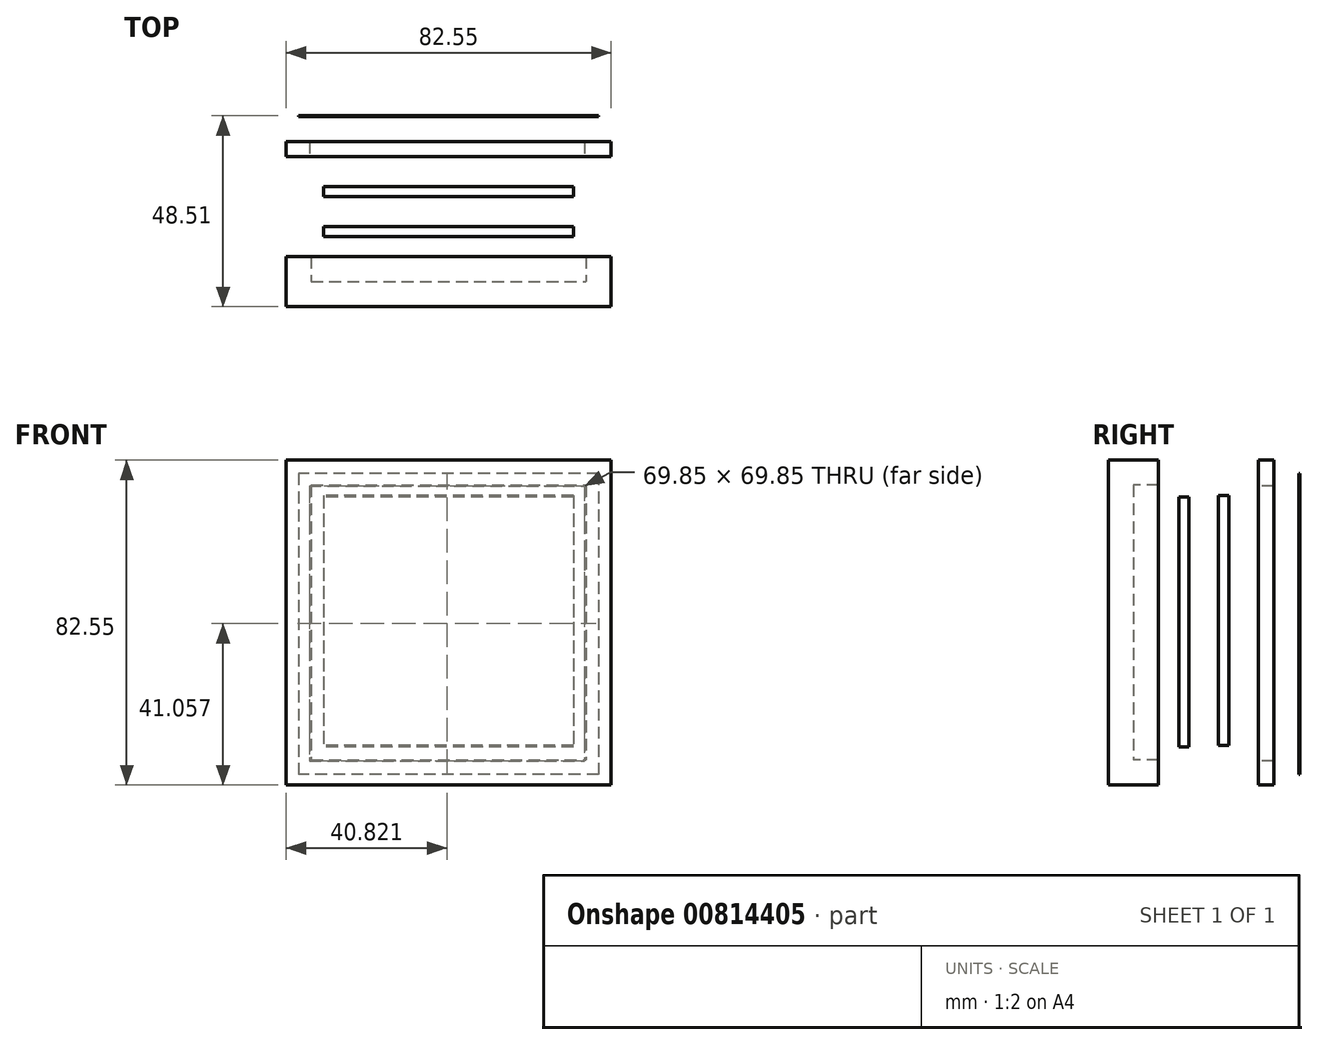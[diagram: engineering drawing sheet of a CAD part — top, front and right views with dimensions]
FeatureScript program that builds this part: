
annotation { "Feature Type Name" : "Feature", "Feature Type Description" : "" }
export const myFeature = defineFeature(function(context is Context, id is Id, definition is map)
    precondition{}
    {
        {
            var Q0;
            Q0=qCreatedBy(makeId("Front.planeOp"),FACE);
            var sketch = newSketch(context, id + "F0", { "sketchPlane" : qUnion([Q0])});
            skLineSegment(sketch, "E0.bottom", {"start": v(0, 0) * mm, "end": v(82.55, 0) * mm});
            skLineSegment(sketch, "E0.top", {"start": v(0, -82.55) * mm, "end": v(82.55, -82.55) * mm});
            skLineSegment(sketch, "E0.left", {"start": v(0, 0) * mm, "end": v(0, -82.55) * mm});
            skLineSegment(sketch, "E0.right", {"start": v(82.55, 0) * mm, "end": v(82.55, -82.55) * mm});
            skLineSegment(sketch, "E1.bottom", {"start": v(6.35, -6.35) * mm, "end": v(76.2, -6.35) * mm});
            skLineSegment(sketch, "E1.top", {"start": v(6.35, -76.2) * mm, "end": v(76.2, -76.2) * mm});
            skLineSegment(sketch, "E1.left", {"start": v(6.35, -6.35) * mm, "end": v(6.35, -76.2) * mm});
            skLineSegment(sketch, "E1.right", {"start": v(76.2, -6.35) * mm, "end": v(76.2, -76.2) * mm});
            skSolve(sketch);
        }
        {
            var Q0;
            Q0=makeQuery(id+"F0.imprint","IMPRINT",FACE,{"disambiguationData":[TD([[makeQuery(id+"F0.imprint","IMPRINT",EDGE,{"derivedFrom":sQuery(id+"F0.wireOp",EDGE,"E1.bottom")}),-1.0]])]});
            extrude(context, id + "F1", {"entities" : qUnion([Q0]), "oppositeDirection" : true, "depth" : 6.35 * mm, "offsetDistance" : 25.4 * mm});
        }
        {
            var Q0;
            Q0=makeQuery(id+"F0.imprint","IMPRINT",FACE,{"disambiguationData":[TD([[makeQuery(id+"F0.imprint","IMPRINT",EDGE,{"derivedFrom":sQuery(id+"F0.wireOp",EDGE,"E0.bottom")}),-1.0]])]});
            extrude(context, id + "F2", {"entities" : qUnion([Q0]), "operationType" : NewBodyOperationType.ADD, "oppositeDirection" : true, "depth" : 12.7 * mm, "offsetDistance" : 25.4 * mm});
        }
        {
            var Q0;
            Q0=makeQuery(id+"F2.opExtrude","CAP_FACE",FACE,{"disambiguationData":[OSD([sQuery(id+"F0.wireOp",EDGE,"E0.bottom"),sQuery(id+"F0.wireOp",EDGE,"E0.top"),sQuery(id+"F0.wireOp",EDGE,"E0.left"),sQuery(id+"F0.wireOp",EDGE,"E0.right"),sQuery(id+"F0.wireOp",EDGE,"E1.bottom"),sQuery(id+"F0.wireOp",EDGE,"E1.top"),sQuery(id+"F0.wireOp",EDGE,"E1.left"),sQuery(id+"F0.wireOp",EDGE,"E1.right")])],"isStart":false});
            cPlane(context, id + "F3", {"entities" : qUnion([Q0]), "cplaneType" : CPlaneType.OFFSET, "offset" : 5.08 * mm, "width" : 152.4 * mm, "height" : 152.4 * mm});
        }
        {
            var Q0;
            Q0=qCreatedBy(id+"F3.planeOp",FACE);
            var sketch = newSketch(context, id + "F4", { "sketchPlane" : qUnion([Q0])});
            skLineSegment(sketch, "E2.bottom", {"start": v(-72.97, -9.31) * mm, "end": v(-9.47, -9.31) * mm});
            skLineSegment(sketch, "E2.top", {"start": v(-72.97, -72.81) * mm, "end": v(-9.47, -72.81) * mm});
            skLineSegment(sketch, "E2.left", {"start": v(-72.97, -9.31) * mm, "end": v(-72.97, -72.81) * mm});
            skLineSegment(sketch, "E2.right", {"start": v(-9.47, -9.31) * mm, "end": v(-9.47, -72.81) * mm});
            skSolve(sketch);
        }
        {
            var Q0;
            Q0 = qSketchRegion(id + "F4", true);
            extrude(context, id + "F5", {"entities" : qUnion([Q0]), "depth" : 2.54 * mm, "offsetDistance" : 25.4 * mm});
        }
        {
            var Q0;
            Q0=makeQuery(id+"F5.opExtrude","CAP_FACE",FACE,{"disambiguationData":[OSD([sQuery(id+"F4.wireOp",EDGE,"E2.bottom"),sQuery(id+"F4.wireOp",EDGE,"E2.top"),sQuery(id+"F4.wireOp",EDGE,"E2.left"),sQuery(id+"F4.wireOp",EDGE,"E2.right")])],"isStart":false});
            cPlane(context, id + "F6", {"entities" : qUnion([Q0]), "cplaneType" : CPlaneType.OFFSET, "offset" : 7.62 * mm, "width" : 152.4 * mm, "height" : 152.4 * mm});
        }
        {
            var Q0;
            Q0=qCreatedBy(id+"F6.planeOp",FACE);
            var sketch = newSketch(context, id + "F7", { "sketchPlane" : qUnion([Q0])});
            skLineSegment(sketch, "E3.bottom", {"start": v(-72.94, -8.95) * mm, "end": v(-9.44, -8.95) * mm});
            skLineSegment(sketch, "E3.top", {"start": v(-72.94, -72.45) * mm, "end": v(-9.44, -72.45) * mm});
            skLineSegment(sketch, "E3.left", {"start": v(-72.94, -8.95) * mm, "end": v(-72.94, -72.45) * mm});
            skLineSegment(sketch, "E3.right", {"start": v(-9.44, -8.95) * mm, "end": v(-9.44, -72.45) * mm});
            skSolve(sketch);
        }
        {
            var Q0;
            Q0=makeQuery(id+"F7.imprint","IMPRINT",FACE,{"disambiguationData":[TD([[makeQuery(id+"F7.imprint","IMPRINT",EDGE,{"derivedFrom":sQuery(id+"F7.wireOp",EDGE,"E3.bottom")}),-1.0]])]});
            extrude(context, id + "F8", {"entities" : qUnion([Q0]), "depth" : 2.54 * mm, "offsetDistance" : 25.4 * mm});
        }
        {
            var Q0;
            Q0=makeQuery(id+"F8.opExtrude","CAP_FACE",FACE,{"disambiguationData":[OSD([sQuery(id+"F7.wireOp",EDGE,"E3.bottom"),sQuery(id+"F7.wireOp",EDGE,"E3.top"),sQuery(id+"F7.wireOp",EDGE,"E3.left"),sQuery(id+"F7.wireOp",EDGE,"E3.right")])],"isStart":false});
            cPlane(context, id + "F9", {"entities" : qUnion([Q0]), "cplaneType" : CPlaneType.OFFSET, "offset" : 7.62 * mm, "width" : 152.4 * mm, "height" : 152.4 * mm});
        }
        {
            var Q0;
            Q0=qCreatedBy(id+"F9.planeOp",FACE);
            var sketch = newSketch(context, id + "F10", { "sketchPlane" : qUnion([Q0])});
            skLineSegment(sketch, "E4.bottom", {"start": v(0, 0) * mm, "end": v(-82.55, 0) * mm});
            skLineSegment(sketch, "E4.top", {"start": v(0, -82.55) * mm, "end": v(-82.55, -82.55) * mm});
            skLineSegment(sketch, "E4.left", {"start": v(0, 0) * mm, "end": v(0, -82.55) * mm});
            skLineSegment(sketch, "E4.right", {"start": v(-82.55, 0) * mm, "end": v(-82.55, -82.55) * mm});
            skLineSegment(sketch, "E5.bottom", {"start": v(-5.9, -6.57) * mm, "end": v(-75.75, -6.57) * mm});
            skLineSegment(sketch, "E5.top", {"start": v(-5.9, -76.42) * mm, "end": v(-75.75, -76.42) * mm});
            skLineSegment(sketch, "E5.left", {"start": v(-5.9, -6.57) * mm, "end": v(-5.9, -76.42) * mm});
            skLineSegment(sketch, "E5.right", {"start": v(-75.75, -6.57) * mm, "end": v(-75.75, -76.42) * mm});
            skSolve(sketch);
        }
        {
            var Q0;
            Q0=makeQuery(id+"F10.imprint","IMPRINT",FACE,{"disambiguationData":[TD([[makeQuery(id+"F10.imprint","IMPRINT",EDGE,{"derivedFrom":sQuery(id+"F10.wireOp",EDGE,"E4.bottom")}),1.0]])]});
            extrude(context, id + "F11", {"entities" : qUnion([Q0]), "depth" : 3.8 * mm, "offsetDistance" : 25.4 * mm});
        }
        {
            var Q0;
            Q0=makeQuery(id+"F11.opExtrude","CAP_FACE",FACE,{"disambiguationData":[OSD([sQuery(id+"F10.wireOp",EDGE,"E4.bottom"),sQuery(id+"F10.wireOp",EDGE,"E4.top"),sQuery(id+"F10.wireOp",EDGE,"E4.left"),sQuery(id+"F10.wireOp",EDGE,"E4.right"),sQuery(id+"F10.wireOp",EDGE,"E5.bottom"),sQuery(id+"F10.wireOp",EDGE,"E5.top"),sQuery(id+"F10.wireOp",EDGE,"E5.left"),sQuery(id+"F10.wireOp",EDGE,"E5.right")])],"isStart":false});
            cPlane(context, id + "F12", {"entities" : qUnion([Q0]), "cplaneType" : CPlaneType.OFFSET, "offset" : 6.35 * mm, "width" : 152.4 * mm, "height" : 152.4 * mm});
        }
        {
            var Q0;
            Q0=qCreatedBy(id+"F12.planeOp",FACE);
            var sketch = newSketch(context, id + "F13", { "sketchPlane" : qUnion([Q0])});
            skLineSegment(sketch, "E6.bottom", {"start": v(-79.38, -3.34) * mm, "end": v(-3.1, -3.34) * mm});
            skLineSegment(sketch, "E6.top", {"start": v(-79.38, -79.84) * mm, "end": v(-3.1, -79.84) * mm});
            skLineSegment(sketch, "E6.left", {"start": v(-79.38, -3.34) * mm, "end": v(-79.38, -79.84) * mm});
            skLineSegment(sketch, "E6.right", {"start": v(-3.1, -3.34) * mm, "end": v(-3.1, -79.84) * mm});
            skSolve(sketch);
        }
        {
            var Q0;
            Q0=makeQuery(id+"F13.imprint","IMPRINT",FACE,{"disambiguationData":[TD([[makeQuery(id+"F13.imprint","IMPRINT",EDGE,{"derivedFrom":sQuery(id+"F13.wireOp",EDGE,"E6.bottom")}),-1.0]])]});
            extrude(context, id + "F14", {"entities" : qUnion([Q0]), "depth" : 0.25 * mm, "offsetDistance" : 25.4 * mm});
        }
    });
